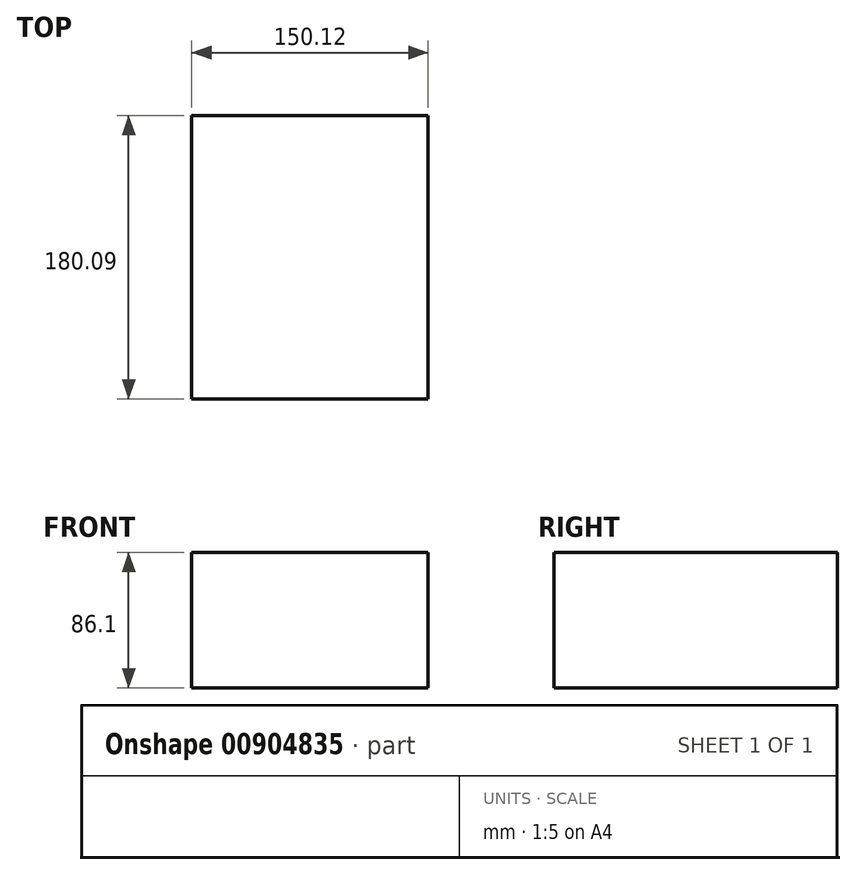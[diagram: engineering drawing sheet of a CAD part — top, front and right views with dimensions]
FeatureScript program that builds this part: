
annotation { "Feature Type Name" : "Feature", "Feature Type Description" : "" }
export const myFeature = defineFeature(function(context is Context, id is Id, definition is map)
    precondition{}
    {
        {
            var Q0;
            Q0=qCreatedBy(makeId("Front.planeOp"),FACE);
            var sketch = newSketch(context, id + "F0", { "sketchPlane" : qUnion([Q0])});
            skLineSegment(sketch, "E0.bottom", {"start": v(75.06, -43.05) * mm, "end": v(-75.06, -43.05) * mm});
            skLineSegment(sketch, "E0.top", {"start": v(75.06, 43.05) * mm, "end": v(-75.06, 43.05) * mm});
            skLineSegment(sketch, "E0.left", {"start": v(75.06, -43.05) * mm, "end": v(75.06, 43.05) * mm});
            skLineSegment(sketch, "E0.right", {"start": v(-75.06, -43.05) * mm, "end": v(-75.06, 43.05) * mm});
            skPoint(sketch, "E0.middle", {"position": v(0, 0) * mm});
            skSolve(sketch);
        }
        {
            var Q0;
            Q0=makeQuery(id+"F0.imprint","IMPRINT",FACE,{"disambiguationData":[TD([[makeQuery(id+"F0.imprint","IMPRINT",EDGE,{"derivedFrom":sQuery(id+"F0.wireOp",EDGE,"E0.bottom")}),-1.0]])]});
            extrude(context, id + "F1", {"entities" : qUnion([Q0]), "depth" : 180.1 * mm, "offsetDistance" : 25.4 * mm});
        }
    });
